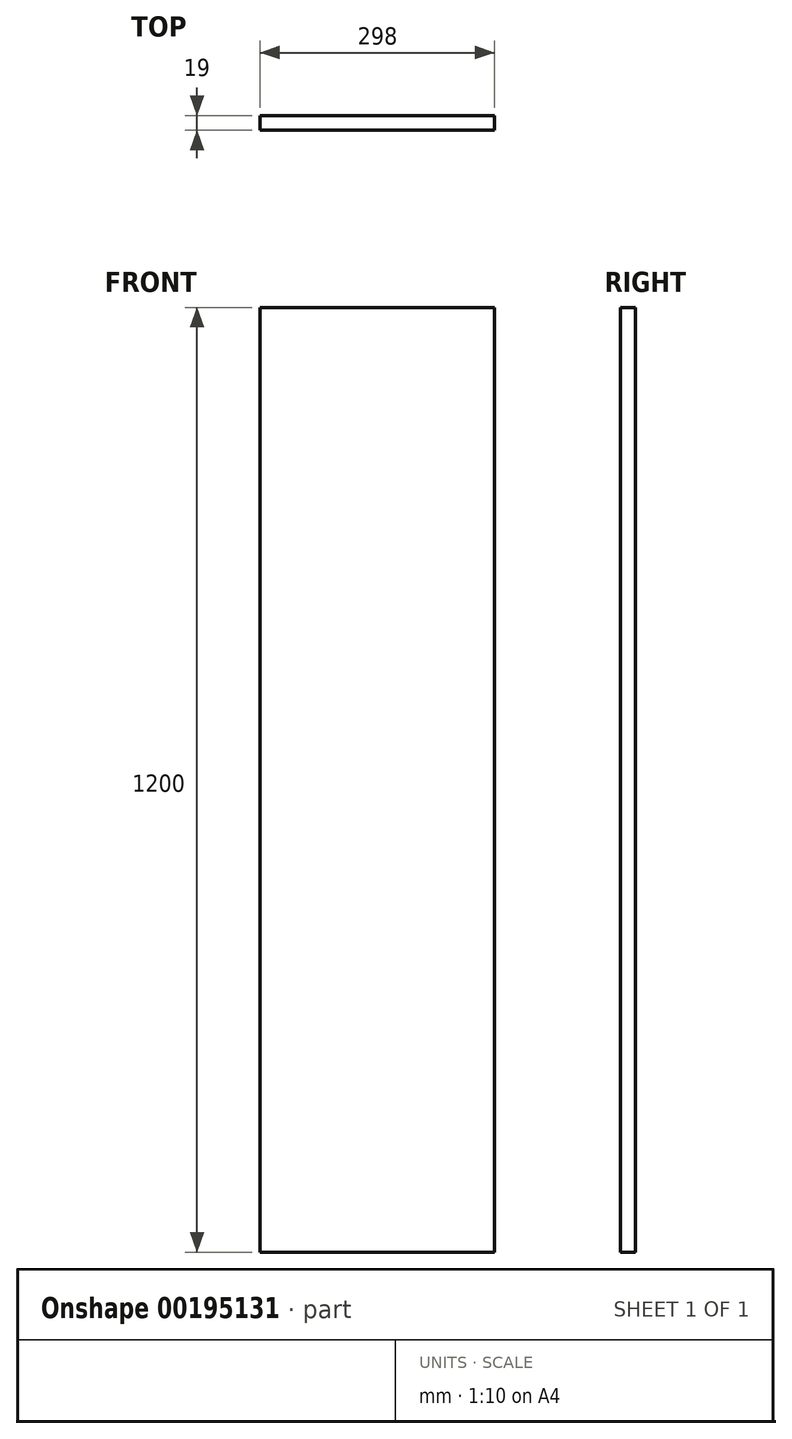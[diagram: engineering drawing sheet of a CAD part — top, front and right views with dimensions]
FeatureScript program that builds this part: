
annotation { "Feature Type Name" : "Feature", "Feature Type Description" : "" }
export const myFeature = defineFeature(function(context is Context, id is Id, definition is map)
    precondition{}
    {
        {
            var Q0;
            Q0=qCreatedBy(makeId("Front.planeOp"),FACE);
            var sketch = newSketch(context, id + "F0", { "sketchPlane" : qUnion([Q0])});
            skLineSegment(sketch, "E0.bottom", {"start": v(-268.22, 603.38) * mm, "end": v(29.78, 603.38) * mm});
            skLineSegment(sketch, "E0.top", {"start": v(-268.22, -596.62) * mm, "end": v(29.78, -596.62) * mm});
            skLineSegment(sketch, "E0.left", {"start": v(-268.22, 603.38) * mm, "end": v(-268.22, -596.62) * mm});
            skLineSegment(sketch, "E0.right", {"start": v(29.78, 603.38) * mm, "end": v(29.78, -596.62) * mm});
            skSolve(sketch);
        }
        {
            var Q0;
            Q0=makeQuery(id+"F0.imprint","IMPRINT",FACE,{"disambiguationData":[TD([[makeQuery(id+"F0.imprint","IMPRINT",EDGE,{"derivedFrom":sQuery(id+"F0.wireOp",EDGE,"E0.bottom")}),-1.0]])]});
            extrude(context, id + "F1", {"entities" : qUnion([Q0]), "depth" : 19 * mm});
        }
    });
